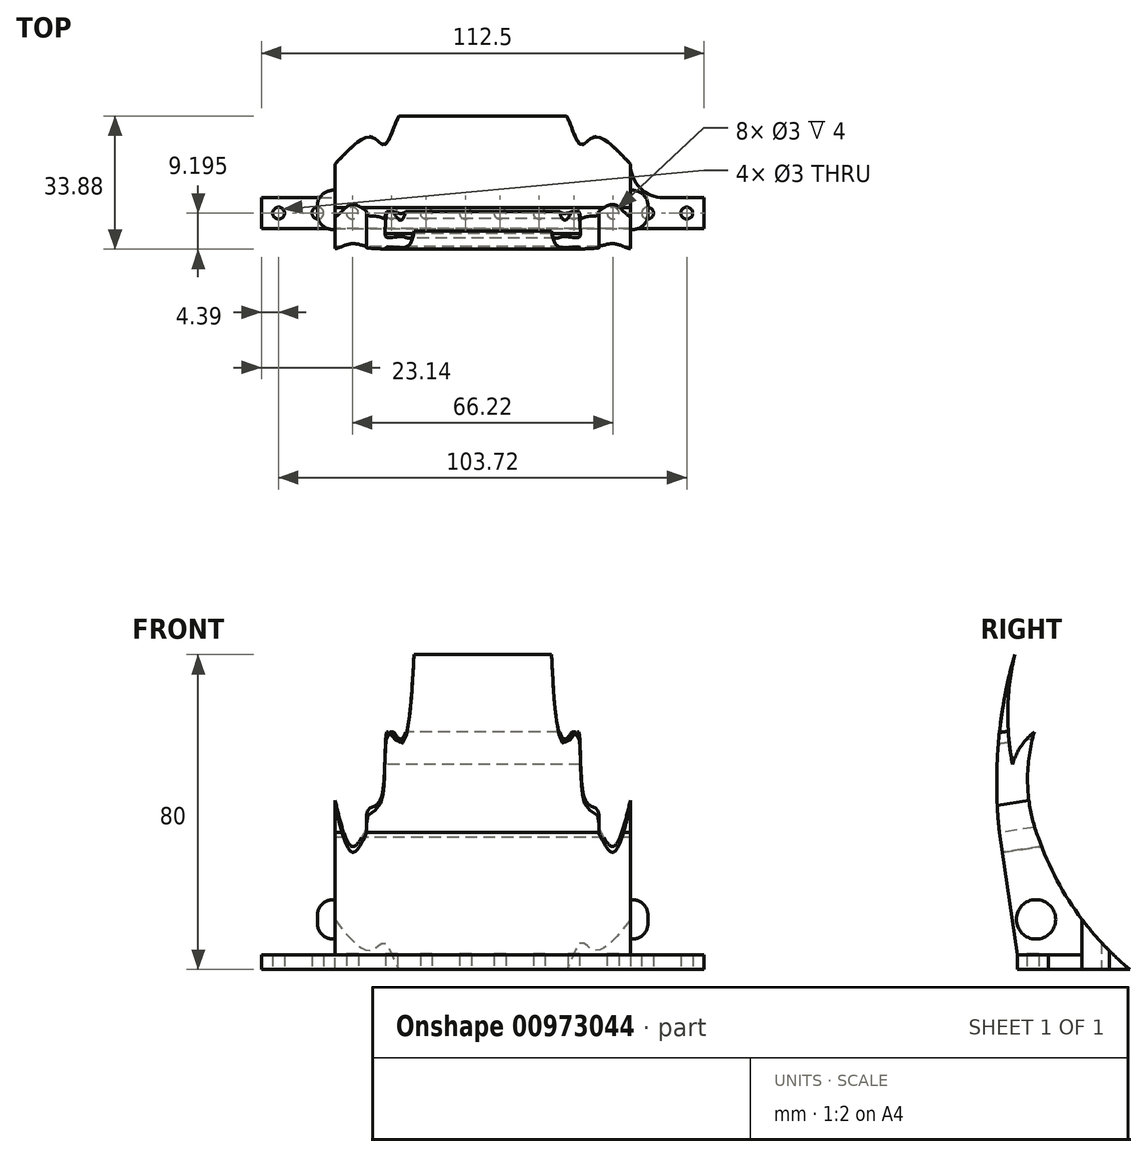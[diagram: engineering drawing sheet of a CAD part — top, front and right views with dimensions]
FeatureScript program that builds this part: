
annotation { "Feature Type Name" : "Feature", "Feature Type Description" : "" }
export const myFeature = defineFeature(function(context is Context, id is Id, definition is map)
    precondition{}
    {
        {
            var Q0;
            Q0=qCreatedBy(makeId("Top.planeOp"),FACE);
            var sketch = newSketch(context, id + "F0", { "sketchPlane" : qUnion([Q0])});
            skLineSegment(sketch, "E0.bottom", {"start": v(-38.78, 3.53) * mm, "end": v(73.72, 3.53) * mm});
            skLineSegment(sketch, "E0.top", {"start": v(-38.78, -4.36) * mm, "end": v(73.72, -4.36) * mm});
            skLineSegment(sketch, "E0.left", {"start": v(-38.78, 3.53) * mm, "end": v(-38.78, -4.36) * mm});
            skLineSegment(sketch, "E0.right", {"start": v(73.72, 3.53) * mm, "end": v(73.72, -4.36) * mm});
            skLineSegment(sketch, "E1", {"start": v(-20.03, 3.53) * mm, "end": v(-20.03, -4.36) * mm, "construction": true});
            skLineSegment(sketch, "E2", {"start": v(54.97, 3.53) * mm, "end": v(54.97, -4.36) * mm, "construction": true});
            skLineSegment(sketch, "E3", {"start": v(-38.78, -0.42) * mm, "end": v(73.72, -0.42) * mm, "construction": true});
            skCircle(sketch, "E4", {"center": v(-34.4, -0.42) * mm, "radius": 1.5 * mm});
            skCircle(sketch, "E5", {"center": v(-24.42, -0.42) * mm, "radius": 1.5 * mm});
            skCircle(sketch, "E6", {"center": v(59.36, -0.42) * mm, "radius": 1.5 * mm});
            skCircle(sketch, "E7", {"center": v(69.33, -0.42) * mm, "radius": 1.5 * mm});
            skLineSegment(sketch, "E8", {"start": v(-29.4, 3.53) * mm, "end": v(-29.4, -4.36) * mm, "construction": true});
            skLineSegment(sketch, "E9", {"start": v(-20.03, 3.53) * mm, "end": v(-38.78, 3.53) * mm});
            skLineSegment(sketch, "E10", {"start": v(54.97, 3.53) * mm, "end": v(73.72, 3.53) * mm, "construction": true});
            skLineSegment(sketch, "E11", {"start": v(64.35, 3.53) * mm, "end": v(64.35, -4.36) * mm, "construction": true});
            skLineSegment(sketch, "E12", {"start": v(-32.9, -0.42) * mm, "end": v(-25.92, -0.42) * mm});
            skPoint(sketch, "E13", {"position": v(-29.4, -0.42) * mm});
            skLineSegment(sketch, "E14", {"start": v(60.86, -0.42) * mm, "end": v(67.83, -0.42) * mm, "construction": true});
            skPoint(sketch, "E15", {"position": v(64.35, -0.42) * mm});
            skCircle(sketch, "E16.1.0.0", {"center": v(-15.64, -0.42) * mm, "radius": 1.5 * mm});
            skCircle(sketch, "E16.1.0.1", {"center": v(-5.67, -0.42) * mm, "radius": 1.5 * mm});
            skCircle(sketch, "E16.2.0.0", {"center": v(3.1, -0.42) * mm, "radius": 1.5 * mm});
            skCircle(sketch, "E16.2.0.1", {"center": v(13.08, -0.42) * mm, "radius": 1.5 * mm});
            skCircle(sketch, "E16.3.0.0", {"center": v(21.86, -0.42) * mm, "radius": 1.5 * mm});
            skCircle(sketch, "E16.3.0.1", {"center": v(31.83, -0.42) * mm, "radius": 1.5 * mm});
            skCircle(sketch, "E16.4.0.0", {"center": v(40.6, -0.42) * mm, "radius": 1.5 * mm});
            skCircle(sketch, "E16.4.0.1", {"center": v(50.58, -0.42) * mm, "radius": 1.5 * mm});
            skLineSegment(sketch, "E16.direction1", {"start": v(-34.4, -0.42) * mm, "end": v(-15.64, -0.42) * mm, "construction": true});
            skSolve(sketch);
        }
        {
            var Q0;
            Q0 = qSketchRegion(id + "F0", true);
            extrude(context, id + "F1", {"entities" : qUnion([Q0]), "depth" : 3.75 * mm, "offsetDistance" : 25 * mm});
        }
        {
            var Q0;
            Q0=makeQuery(id+"F1.opExtrude","CAP_FACE",FACE,{"disambiguationData":[OSD([sQuery(id+"F0.wireOp",EDGE,"E0.bottom"),sQuery(id+"F0.wireOp",EDGE,"E0.top"),sQuery(id+"F0.wireOp",EDGE,"E0.left"),sQuery(id+"F0.wireOp",EDGE,"E0.right"),sQuery(id+"F0.wireOp",EDGE,"E4"),sQuery(id+"F0.wireOp",EDGE,"E5"),sQuery(id+"F0.wireOp",EDGE,"E6"),sQuery(id+"F0.wireOp",EDGE,"E7"),sQuery(id+"F0.wireOp",EDGE,"E9")])],"isStart":false});
            var sketch = newSketch(context, id + "F2", { "sketchPlane" : qUnion([Q0])});
            skLineSegment(sketch, "E17.bottom", {"start": v(-20.03, 3.53) * mm, "end": v(54.97, 3.53) * mm});
            skLineSegment(sketch, "E17.top", {"start": v(-20.03, -4.36) * mm, "end": v(54.97, -4.36) * mm});
            skLineSegment(sketch, "E17.left", {"start": v(-20.03, 3.53) * mm, "end": v(-20.03, -4.36) * mm});
            skLineSegment(sketch, "E17.right", {"start": v(54.97, 3.53) * mm, "end": v(54.97, -4.36) * mm});
            skSolve(sketch);
        }
        {
            var Q0;
            Q0 = qSketchRegion(id + "F2", true);
            extrude(context, id + "F3", {"entities" : qUnion([Q0]), "operationType" : NewBodyOperationType.ADD, "depth" : 10 * mm, "offsetDistance" : 25 * mm});
        }
        {
            var Q0;
            Q0=makeQuery(id+"F3.boolean.opBoolean","MERGE",FACE,{"derivedFrom":[makeQuery(id+"F1.opExtrude","SWEPT_FACE",FACE,{"disambiguationData":[OSD([sQuery(id+"F0.wireOp",EDGE,"E0.bottom"),sQuery(id+"F0.wireOp",EDGE,"E9")])]}),makeQuery(id+"F3.opExtrude","SWEPT_FACE",FACE,{"disambiguationData":[OSD([sQuery(id+"F2.wireOp",EDGE,"E17.bottom")])]})]});
            var sketch = newSketch(context, id + "F4", { "sketchPlane" : qUnion([Q0])});
            skLineSegment(sketch, "E18.bottom", {"start": v(-54.97, 13.75) * mm, "end": v(20.03, 13.75) * mm});
            skLineSegment(sketch, "E18.top", {"start": v(-54.97, 0) * mm, "end": v(20.03, 0) * mm});
            skLineSegment(sketch, "E18.left", {"start": v(20.03, 0) * mm, "end": v(20.03, 13.75) * mm});
            skLineSegment(sketch, "E18.right", {"start": v(-54.97, 0) * mm, "end": v(-54.97, 13.75) * mm});
            skSolve(sketch);
        }
        {
            var Q0;
            Q0 = qSketchRegion(id + "F4", true);
            extrude(context, id + "F5", {"entities" : qUnion([Q0]), "operationType" : NewBodyOperationType.ADD, "depth" : 25 * mm, "offsetDistance" : 25 * mm});
        }
        {
            var Q0;
            Q0=makeQuery(id+"F5.boolean.opBoolean","MERGE",FACE,{"derivedFrom":[makeQuery(id+"F3.opExtrude","SWEPT_FACE",FACE,{"disambiguationData":[OSD([sQuery(id+"F2.wireOp",EDGE,"E17.left")])]}),makeQuery(id+"F5.opExtrude","SWEPT_FACE",FACE,{"disambiguationData":[OSD([sQuery(id+"F4.wireOp",EDGE,"E18.left")])]})]});
            var sketch = newSketch(context, id + "F6", { "sketchPlane" : qUnion([Q0])});
            skFitSpline(sketch, "E19", {"points": [v(-28.53, 0) * mm, v(-27.7, 3) * mm, v(-21.04, 9.75) * mm, v(-22.48, 11.13) * mm, v(-12.08, 13.75) * mm], "startDerivative": vector(-1.4, 14.45) * mm, "endDerivative": vector(46.88, 7.86) * mm});
            skSolve(sketch);
        }
        {
            var Q0;
            {var subQ0=sQuery(id+"F6.wireOp",EDGE,"E19");var subQ1=sQuery(id+"F4.wireOp",EDGE,"E18.left");var subQ4=makeQuery(id+"F5.opExtrude","CAP_EDGE",EDGE,{"disambiguationData":[OSD([subQ1])],"isStart":false});var subQ5=makeQuery(id+"F6.imprint","INTERSECT",VERTEX,{"derivedFrom":[subQ4,subQ0]});Q0=makeQuery(id+"F6.imprint","IMPRINT",FACE,{"disambiguationData":[TD([[makeQuery(id+"F6.imprint","IMPRINT",EDGE,{"disambiguationData":[TD([[subQ5,-1.0]])],"derivedFrom":subQ0}),1.0]])]});}
            extrude(context, id + "F7", {"entities" : qUnion([Q0]), "operationType" : NewBodyOperationType.REMOVE, "oppositeDirection" : true, "depth" : 108.8 * mm, "offsetDistance" : 25 * mm});
        }
        {
            var Q0;
            Q0=makeQuery(id+"F5.boolean.opBoolean","MERGE",FACE,{"derivedFrom":[makeQuery(id+"F3.opExtrude","CAP_FACE",FACE,{"disambiguationData":[OSD([sQuery(id+"F2.wireOp",EDGE,"E17.bottom"),sQuery(id+"F2.wireOp",EDGE,"E17.top"),sQuery(id+"F2.wireOp",EDGE,"E17.left"),sQuery(id+"F2.wireOp",EDGE,"E17.right")])],"isStart":false}),makeQuery(id+"F5.opExtrude","SWEPT_FACE",FACE,{"disambiguationData":[OSD([sQuery(id+"F4.wireOp",EDGE,"E18.bottom")])]})]});
            var sketch = newSketch(context, id + "F8", { "sketchPlane" : qUnion([Q0])});
            skFitSpline(sketch, "E20", {"points": [v(-20.03, 12.08) * mm, v(-10.74, 18.9) * mm, v(-7.44, 17) * mm, v(-1.88, 26.86) * mm, v(6.82, 24.75) * mm, v(17.47, 28.53) * mm], "startDerivative": vector(45.64, 47.07) * mm, "endDerivative": vector(40.7, 21.22) * mm});
            skLineSegment(sketch, "E21", {"start": v(17.47, -4.36) * mm, "end": v(17.47, 28.53) * mm, "construction": true});
            skFitSpline(sketch, "E22.MirrorCS", {"points": [v(54.97, 12.08) * mm, v(45.68, 18.9) * mm, v(42.38, 17) * mm, v(36.82, 26.86) * mm, v(28.12, 24.75) * mm, v(17.47, 28.53) * mm], "startDerivative": vector(-45.64, 47.07) * mm, "endDerivative": vector(-40.7, 21.22) * mm});
            skLineSegment(sketch, "E23.0", {"start": v(54.97, 28.53) * mm, "end": v(-20.03, 28.53) * mm});
            skLineSegment(sketch, "E24.0", {"start": v(54.97, 28.53) * mm, "end": v(54.97, 3.53) * mm});
            skLineSegment(sketch, "E24.1", {"start": v(-20.03, 28.53) * mm, "end": v(-20.03, 3.53) * mm});
            skSolve(sketch);
        }
        {
            var Q0;
            Q0 = qSketchRegion(id + "F8", true);
            extrude(context, id + "F9", {"entities" : qUnion([Q0]), "operationType" : NewBodyOperationType.REMOVE, "oppositeDirection" : true, "depth" : 25 * mm, "offsetDistance" : 25 * mm});
        }
        {
            var Q0;
            Q0=makeQuery(id+"F5.boolean.opBoolean","MERGE",FACE,{"derivedFrom":[makeQuery(id+"F3.opExtrude","CAP_FACE",FACE,{"disambiguationData":[OSD([sQuery(id+"F2.wireOp",EDGE,"E17.bottom"),sQuery(id+"F2.wireOp",EDGE,"E17.top"),sQuery(id+"F2.wireOp",EDGE,"E17.left"),sQuery(id+"F2.wireOp",EDGE,"E17.right")])],"isStart":false}),makeQuery(id+"F5.opExtrude","SWEPT_FACE",FACE,{"disambiguationData":[OSD([sQuery(id+"F4.wireOp",EDGE,"E18.bottom")])]})]});
            var sketch = newSketch(context, id + "F10", { "sketchPlane" : qUnion([Q0])});
            skLineSegment(sketch, "E25.bottom", {"start": v(-6.29, -4.36) * mm, "end": v(40.42, -4.36) * mm});
            skLineSegment(sketch, "E25.top", {"start": v(-6.29, 12.08) * mm, "end": v(40.42, 12.08) * mm, "construction": true});
            skLineSegment(sketch, "E25.left", {"start": v(-6.29, -4.36) * mm, "end": v(-6.29, 12.08) * mm});
            skLineSegment(sketch, "E25.right", {"start": v(40.42, -4.36) * mm, "end": v(40.42, 12.08) * mm});
            skLineSegment(sketch, "E26", {"start": v(-6.29, 12.08) * mm, "end": v(17.07, 17.99) * mm});
            skLineSegment(sketch, "E27", {"start": v(17.07, 17.99) * mm, "end": v(40.42, 12.08) * mm});
            skLineSegment(sketch, "E28", {"start": v(17.07, -4.36) * mm, "end": v(17.07, 30.33) * mm});
            skSolve(sketch);
        }
        {
            var Q0;
            {var subQ0=sQuery(id+"F10.wireOp",EDGE,"E25.right");Q0=makeQuery(id+"F10.imprint","IMPRINT",FACE,{"disambiguationData":[TD([[makeQuery(id+"F10.imprint","IMPRINT",EDGE,{"derivedFrom":subQ0}),1.0]])]});}
            var Q1;
            {var subQ0=sQuery(id+"F10.wireOp",EDGE,"E25.left");Q1=makeQuery(id+"F10.imprint","IMPRINT",FACE,{"disambiguationData":[TD([[makeQuery(id+"F10.imprint","IMPRINT",EDGE,{"derivedFrom":subQ0}),-1.0]])]});}
            var Q2;
            {var subQ0=sQuery(id+"F10.wireOp",EDGE,"E27");Q2=makeQuery(id+"F10.imprint","IMPRINT",FACE,{"disambiguationData":[TD([[makeQuery(id+"F10.imprint","IMPRINT",EDGE,{"derivedFrom":subQ0}),-1.0]])]});}
            var Q3;
            {var subQ0=sQuery(id+"F10.wireOp",EDGE,"E26");Q3=makeQuery(id+"F10.imprint","IMPRINT",FACE,{"disambiguationData":[TD([[makeQuery(id+"F10.imprint","IMPRINT",EDGE,{"derivedFrom":subQ0}),-1.0]])]});}
            extrude(context, id + "F11", {"entities" : qUnion([Q0, Q1, Q2, Q3]), "operationType" : NewBodyOperationType.ADD, "depth" : 5 * mm, "offsetDistance" : 25 * mm});
        }
        {
            var Q0;
            Q0=makeQuery(id+"F11.opExtrude","CAP_EDGE",EDGE,{"disambiguationData":[OSD([sQuery(id+"F10.wireOp",EDGE,"E25.left")])],"isStart":true});
            var Q1;
            Q1=makeQuery(id+"F11.opExtrude","CAP_EDGE",EDGE,{"disambiguationData":[OSD([sQuery(id+"F10.wireOp",EDGE,"E25.right")])],"isStart":true});
            fillet(context, id + "F12", {"entities" : qUnion([Q0, Q1]), "radius" : 21.25 * mm, "tangentPropagation" : true, "allowEdgeOverflow" : false});
        }
        {
            var Q0;
            {var subQ0=sQuery(id+"F10.wireOp",EDGE,"E25.left");Q0=makeQuery(id+"F12.opFillet","BLEND_EDGE",EDGE,{"blendedFrom":[makeQuery(id+"F11.opExtrude","CAP_EDGE",EDGE,{"disambiguationData":[OSD([subQ0])],"isStart":true}),makeQuery(id+"F11.opExtrude","CAP_FACE",FACE,{"disambiguationData":[OSD([sQuery(id+"F10.wireOp",EDGE,"E25.bottom"),subQ0,sQuery(id+"F10.wireOp",EDGE,"E25.right"),sQuery(id+"F10.wireOp",EDGE,"E26"),sQuery(id+"F10.wireOp",EDGE,"E27")])],"isStart":false})],"blendedInto":[makeQuery(id+"F11.opExtrude","CAP_FACE",FACE,{"disambiguationData":[OSD([sQuery(id+"F10.wireOp",EDGE,"E25.bottom"),subQ0,sQuery(id+"F10.wireOp",EDGE,"E25.right"),sQuery(id+"F10.wireOp",EDGE,"E26"),sQuery(id+"F10.wireOp",EDGE,"E27")])],"isStart":false})]});}
            var Q1;
            {var subQ0=sQuery(id+"F10.wireOp",EDGE,"E26");Q1=makeQuery(id+"FigYtTYyMIsJvTv_1.opChamfer","BLEND_EDGE",EDGE,{"blendedFrom":[makeQuery(id+"F11.opExtrude","CAP_EDGE",EDGE,{"disambiguationData":[OSD([subQ0])],"isStart":false}),makeQuery(id+"F11.opExtrude","CAP_FACE",FACE,{"disambiguationData":[OSD([sQuery(id+"F10.wireOp",EDGE,"E25.bottom"),sQuery(id+"F10.wireOp",EDGE,"E25.left"),sQuery(id+"F10.wireOp",EDGE,"E25.right"),subQ0,sQuery(id+"F10.wireOp",EDGE,"E27")])],"isStart":false})],"blendedInto":[makeQuery(id+"F11.opExtrude","CAP_FACE",FACE,{"disambiguationData":[OSD([sQuery(id+"F10.wireOp",EDGE,"E25.bottom"),sQuery(id+"F10.wireOp",EDGE,"E25.left"),sQuery(id+"F10.wireOp",EDGE,"E25.right"),subQ0,sQuery(id+"F10.wireOp",EDGE,"E27")])],"isStart":false})]});}
            var Q2;
            {var subQ0=sQuery(id+"F10.wireOp",EDGE,"E27");Q2=makeQuery(id+"FigYtTYyMIsJvTv_1.opChamfer","BLEND_EDGE",EDGE,{"blendedFrom":[makeQuery(id+"F11.opExtrude","CAP_EDGE",EDGE,{"disambiguationData":[OSD([subQ0])],"isStart":false}),makeQuery(id+"F11.opExtrude","CAP_FACE",FACE,{"disambiguationData":[OSD([sQuery(id+"F10.wireOp",EDGE,"E25.bottom"),sQuery(id+"F10.wireOp",EDGE,"E25.left"),sQuery(id+"F10.wireOp",EDGE,"E25.right"),sQuery(id+"F10.wireOp",EDGE,"E26"),subQ0])],"isStart":false})],"blendedInto":[makeQuery(id+"F11.opExtrude","CAP_FACE",FACE,{"disambiguationData":[OSD([sQuery(id+"F10.wireOp",EDGE,"E25.bottom"),sQuery(id+"F10.wireOp",EDGE,"E25.left"),sQuery(id+"F10.wireOp",EDGE,"E25.right"),sQuery(id+"F10.wireOp",EDGE,"E26"),subQ0])],"isStart":false})]});}
            var Q3;
            {var subQ0=sQuery(id+"F10.wireOp",EDGE,"E25.right");Q3=makeQuery(id+"F12.opFillet","BLEND_EDGE",EDGE,{"blendedFrom":[makeQuery(id+"F11.opExtrude","CAP_EDGE",EDGE,{"disambiguationData":[OSD([subQ0])],"isStart":true}),makeQuery(id+"F11.opExtrude","CAP_FACE",FACE,{"disambiguationData":[OSD([sQuery(id+"F10.wireOp",EDGE,"E25.bottom"),sQuery(id+"F10.wireOp",EDGE,"E25.left"),subQ0,sQuery(id+"F10.wireOp",EDGE,"E26"),sQuery(id+"F10.wireOp",EDGE,"E27")])],"isStart":false})],"blendedInto":[makeQuery(id+"F11.opExtrude","CAP_FACE",FACE,{"disambiguationData":[OSD([sQuery(id+"F10.wireOp",EDGE,"E25.bottom"),sQuery(id+"F10.wireOp",EDGE,"E25.left"),subQ0,sQuery(id+"F10.wireOp",EDGE,"E26"),sQuery(id+"F10.wireOp",EDGE,"E27")])],"isStart":false})]});}
            fillet(context, id + "F13", {"entities" : qUnion([Q0, Q1, Q2, Q3]), "radius" : 8 * mm, "tangentPropagation" : true, "allowEdgeOverflow" : false});
        }
        {
            var Q0;
            Q0=makeQuery(id+"F5.boolean.opBoolean","MERGE",FACE,{"derivedFrom":[makeQuery(id+"F3.opExtrude","SWEPT_FACE",FACE,{"disambiguationData":[OSD([sQuery(id+"F2.wireOp",EDGE,"E17.left")])]}),makeQuery(id+"F5.opExtrude","SWEPT_FACE",FACE,{"disambiguationData":[OSD([sQuery(id+"F4.wireOp",EDGE,"E18.left")])]})]});
            var sketch = newSketch(context, id + "F14", { "sketchPlane" : qUnion([Q0])});
            skLineSegment(sketch, "E29", {"start": v(4.36, 3.75) * mm, "end": v(8.92, 34.79) * mm});
            skArc(sketch, "E30", {"start": v(8.92, 34.79) * mm, "mid": v(9.18, 57.58) * mm, "end": v(5, 80) * mm});
            skArc(sketch, "E31", {"start": v(-16.96, 13.75) * mm, "mid": v(3.4, 43.77) * mm, "end": v(5, 80) * mm});
            skArc(sketch, "E32", {"start": v(-0.96, 33.55) * mm, "mid": v(1.74, 46.91) * mm, "end": v(0, 60.43) * mm});
            skArc(sketch, "E33", {"start": v(5.58, 52.1) * mm, "mid": v(3.44, 56.7) * mm, "end": v(0, 60.43) * mm});
            skLineSegment(sketch, "E34", {"start": v(-16.96, 13.75) * mm, "end": v(-5.96, 13.75) * mm});
            skLineSegment(sketch, "E35", {"start": v(-5.96, 13.75) * mm, "end": v(-5.96, 0) * mm});
            skLineSegment(sketch, "E36", {"start": v(-5.96, 0) * mm, "end": v(4.36, 0) * mm});
            skLineSegment(sketch, "E37", {"start": v(4.36, 0) * mm, "end": v(4.36, 3.75) * mm});
            skSolve(sketch);
        }
        {
            var Q0;
            Q0 = qSketchRegion(id + "F14", true);
            extrude(context, id + "F15", {"entities" : qUnion([Q0]), "operationType" : NewBodyOperationType.ADD, "oppositeDirection" : true, "depth" : 75 * mm, "offsetDistance" : 25 * mm});
        }
        {
            var Q0;
            Q0=makeQuery(id+"F15.opExtrude","SWEPT_FACE",FACE,{"disambiguationData":[OSD([sQuery(id+"F14.wireOp",EDGE,"E29")])]});
            var sketch = newSketch(context, id + "F16", { "sketchPlane" : qUnion([Q0])});
            skFitSpline(sketch, "E38", {"points": [v(0, 79.88) * mm, v(-3.73, 58.12) * mm, v(-6.47, 60.86) * mm, v(-8.59, 42.78) * mm, v(-11.43, 40.55) * mm, v(-11.99, 35.71) * mm], "startDerivative": vector(-6.1, -121.82) * mm, "endDerivative": vector(2.52, -42.33) * mm});
            skLineSegment(sketch, "E39", {"start": v(17.47, 4.34) * mm, "end": v(17.47, 79.88) * mm, "construction": true});
            skFitSpline(sketch, "E40.MirrorCS", {"points": [v(34.94, 79.88) * mm, v(38.67, 58.12) * mm, v(41.4, 60.86) * mm, v(43.53, 42.78) * mm, v(46.37, 40.55) * mm, v(46.93, 35.71) * mm], "startDerivative": vector(6.1, -121.82) * mm, "endDerivative": vector(-2.52, -42.33) * mm});
            skFitSpline(sketch, "E41", {"points": [v(-11.99, 35.71) * mm, v(-15.59, 30.67) * mm, v(-20.03, 42.66) * mm], "startDerivative": vector(-9.04, -18.97) * mm, "endDerivative": vector(-7.02, 29.96) * mm});
            skFitSpline(sketch, "E42.MirrorCS", {"points": [v(46.93, 35.71) * mm, v(50.53, 30.67) * mm, v(54.97, 42.66) * mm], "startDerivative": vector(9.04, -18.97) * mm, "endDerivative": vector(7.02, 29.96) * mm});
            skLineSegment(sketch, "E43.0", {"start": v(54.97, 79.88) * mm, "end": v(-20.03, 79.88) * mm});
            skLineSegment(sketch, "E43.1", {"start": v(-20.03, 35.71) * mm, "end": v(-20.03, 79.88) * mm});
            skLineSegment(sketch, "E43.2", {"start": v(54.97, 35.71) * mm, "end": v(54.97, 79.88) * mm});
            skSolve(sketch);
        }
        {
            var Q0;
            Q0 = qSketchRegion(id + "F16", true);
            extrude(context, id + "F17", {"entities" : qUnion([Q0]), "operationType" : NewBodyOperationType.REMOVE, "oppositeDirection" : true, "depth" : 25 * mm, "offsetDistance" : 25 * mm});
        }
        {
            var Q0;
            Q0=makeQuery(id+"F11.opExtrude","CAP_FACE",FACE,{"disambiguationData":[OSD([sQuery(id+"F10.wireOp",EDGE,"E25.bottom"),sQuery(id+"F10.wireOp",EDGE,"E25.left"),sQuery(id+"F10.wireOp",EDGE,"E25.right"),sQuery(id+"F10.wireOp",EDGE,"E26"),sQuery(id+"F10.wireOp",EDGE,"E27")])],"isStart":false});
            var sketch = newSketch(context, id + "F18", { "sketchPlane" : qUnion([Q0])});
            skSolve(sketch);
        }
        {
            var Q0;
            Q0=makeQuery(id+"F5.opExtrude","CAP_EDGE",EDGE,{"disambiguationData":[OSD([sQuery(id+"F4.wireOp",EDGE,"E18.right")])],"isStart":true});
            var Q1;
            Q1=makeQuery(id+"F5.opExtrude","CAP_EDGE",EDGE,{"disambiguationData":[OSD([sQuery(id+"F4.wireOp",EDGE,"E18.left")])],"isStart":true});
            fillet(context, id + "F19", {"entities" : qUnion([Q0, Q1]), "radius" : 8.45 * mm, "tangentPropagation" : true, "allowEdgeOverflow" : false});
        }
        {
            var Q0;
            Q0=makeQuery(id+"F0.imprint","IMPRINT",FACE,{"disambiguationData":[TD([[makeQuery(id+"F0.imprint","IMPRINT",EDGE,{"derivedFrom":sQuery(id+"F0.wireOp",EDGE,"E16.1.0.0")}),1.0]])]});
            var Q1;
            Q1=makeQuery(id+"F0.imprint","IMPRINT",FACE,{"disambiguationData":[TD([[makeQuery(id+"F0.imprint","IMPRINT",EDGE,{"derivedFrom":sQuery(id+"F0.wireOp",EDGE,"E16.1.0.1")}),1.0]])]});
            var Q2;
            Q2=makeQuery(id+"F0.imprint","IMPRINT",FACE,{"disambiguationData":[TD([[makeQuery(id+"F0.imprint","IMPRINT",EDGE,{"derivedFrom":sQuery(id+"F0.wireOp",EDGE,"E16.2.0.0")}),1.0]])]});
            var Q3;
            Q3=makeQuery(id+"F0.imprint","IMPRINT",FACE,{"disambiguationData":[TD([[makeQuery(id+"F0.imprint","IMPRINT",EDGE,{"derivedFrom":sQuery(id+"F0.wireOp",EDGE,"E16.2.0.1")}),1.0]])]});
            var Q4;
            Q4=makeQuery(id+"F0.imprint","IMPRINT",FACE,{"disambiguationData":[TD([[makeQuery(id+"F0.imprint","IMPRINT",EDGE,{"derivedFrom":sQuery(id+"F0.wireOp",EDGE,"E16.3.0.0")}),1.0]])]});
            var Q5;
            Q5=makeQuery(id+"F0.imprint","IMPRINT",FACE,{"disambiguationData":[TD([[makeQuery(id+"F0.imprint","IMPRINT",EDGE,{"derivedFrom":sQuery(id+"F0.wireOp",EDGE,"E16.3.0.1")}),1.0]])]});
            var Q6;
            Q6=makeQuery(id+"F0.imprint","IMPRINT",FACE,{"disambiguationData":[TD([[makeQuery(id+"F0.imprint","IMPRINT",EDGE,{"derivedFrom":sQuery(id+"F0.wireOp",EDGE,"E16.4.0.1")}),1.0]])]});
            var Q7;
            Q7=makeQuery(id+"F0.imprint","IMPRINT",FACE,{"disambiguationData":[TD([[makeQuery(id+"F0.imprint","IMPRINT",EDGE,{"derivedFrom":sQuery(id+"F0.wireOp",EDGE,"E16.4.0.0")}),1.0]])]});
            extrude(context, id + "F20", {"entities" : qUnion([Q0, Q1, Q2, Q3, Q4, Q5, Q6, Q7]), "operationType" : NewBodyOperationType.REMOVE, "depth" : 4 * mm, "offsetDistance" : 25 * mm});
        }
        {
            var Q0;
            Q0=makeQuery(id+"F15.boolean.opBoolean","MERGE",FACE,{"derivedFrom":[makeQuery(id+"F5.boolean.opBoolean","MERGE",FACE,{"derivedFrom":[makeQuery(id+"F3.opExtrude","SWEPT_FACE",FACE,{"disambiguationData":[OSD([sQuery(id+"F2.wireOp",EDGE,"E17.left")])]}),makeQuery(id+"F5.opExtrude","SWEPT_FACE",FACE,{"disambiguationData":[OSD([sQuery(id+"F4.wireOp",EDGE,"E18.left")])]})]}),makeQuery(id+"F15.opExtrude","CAP_FACE",FACE,{"disambiguationData":[OSD([sQuery(id+"F14.wireOp",EDGE,"E29"),sQuery(id+"F14.wireOp",EDGE,"E30"),sQuery(id+"F14.wireOp",EDGE,"E31"),sQuery(id+"F14.wireOp",EDGE,"E32"),sQuery(id+"F14.wireOp",EDGE,"E33"),sQuery(id+"F14.wireOp",EDGE,"E34"),sQuery(id+"F14.wireOp",EDGE,"E35"),sQuery(id+"F14.wireOp",EDGE,"E36"),sQuery(id+"F14.wireOp",EDGE,"E37")])],"isStart":true})]});
            var sketch = newSketch(context, id + "F21", { "sketchPlane" : qUnion([Q0])});
            skArc(sketch, "E44", {"start": v(-24.27, 0) * mm, "mid": v(-10.31, 15.18) * mm, "end": v(-0.96, 33.55) * mm});
            skLineSegment(sketch, "E45", {"start": v(-0.96, 33.55) * mm, "end": v(-34.58, 33.55) * mm});
            skLineSegment(sketch, "E46", {"start": v(-34.58, 33.55) * mm, "end": v(-34.58, 0) * mm});
            skLineSegment(sketch, "E47", {"start": v(-34.58, 0) * mm, "end": v(-24.27, 0) * mm});
            skSolve(sketch);
        }
        {
            var Q0;
            Q0 = qSketchRegion(id + "F21", true);
            extrude(context, id + "F22", {"entities" : qUnion([Q0]), "operationType" : NewBodyOperationType.REMOVE, "oppositeDirection" : true, "depth" : 113.6 * mm, "offsetDistance" : 25 * mm});
        }
        {
            var Q0;
            Q0=makeQuery(id+"F15.boolean.opBoolean","MERGE",FACE,{"derivedFrom":[makeQuery(id+"F5.boolean.opBoolean","MERGE",FACE,{"derivedFrom":[makeQuery(id+"F3.opExtrude","SWEPT_FACE",FACE,{"disambiguationData":[OSD([sQuery(id+"F2.wireOp",EDGE,"E17.right")])]}),makeQuery(id+"F5.opExtrude","SWEPT_FACE",FACE,{"disambiguationData":[OSD([sQuery(id+"F4.wireOp",EDGE,"E18.right")])]})]}),makeQuery(id+"F15.opExtrude","CAP_FACE",FACE,{"disambiguationData":[OSD([sQuery(id+"F14.wireOp",EDGE,"E29"),sQuery(id+"F14.wireOp",EDGE,"E30"),sQuery(id+"F14.wireOp",EDGE,"E31"),sQuery(id+"F14.wireOp",EDGE,"E32"),sQuery(id+"F14.wireOp",EDGE,"E33"),sQuery(id+"F14.wireOp",EDGE,"E34"),sQuery(id+"F14.wireOp",EDGE,"E35"),sQuery(id+"F14.wireOp",EDGE,"E36"),sQuery(id+"F14.wireOp",EDGE,"E37")])],"isStart":false})]});
            var sketch = newSketch(context, id + "F23", { "sketchPlane" : qUnion([Q0])});
            skCircle(sketch, "E48", {"center": v(0.38, 12.75) * mm, "radius": 5 * mm});
            skSolve(sketch);
        }
        {
            var Q0;
            Q0 = qSketchRegion(id + "F23", true);
            extrude(context, id + "F24", {"entities" : qUnion([Q0]), "operationType" : NewBodyOperationType.ADD, "depth" : 4.5 * mm, "offsetDistance" : 25 * mm});
        }
        {
            var Q0;
            Q0=makeQuery(id+"F24.opExtrude","CAP_EDGE",EDGE,{"disambiguationData":[OSD([sQuery(id+"F23.wireOp",EDGE,"E48")])],"isStart":false});
            fillet(context, id + "F25", {"entities" : qUnion([Q0]), "radius" : 4 * mm, "tangentPropagation" : true, "allowEdgeOverflow" : false});
        }
        {
            var Q0;
            Q0=makeQuery(id+"F15.boolean.opBoolean","MERGE",FACE,{"derivedFrom":[makeQuery(id+"F5.boolean.opBoolean","MERGE",FACE,{"derivedFrom":[makeQuery(id+"F3.opExtrude","SWEPT_FACE",FACE,{"disambiguationData":[OSD([sQuery(id+"F2.wireOp",EDGE,"E17.left")])]}),makeQuery(id+"F5.opExtrude","SWEPT_FACE",FACE,{"disambiguationData":[OSD([sQuery(id+"F4.wireOp",EDGE,"E18.left")])]})]}),makeQuery(id+"F15.opExtrude","CAP_FACE",FACE,{"disambiguationData":[OSD([sQuery(id+"F14.wireOp",EDGE,"E29"),sQuery(id+"F14.wireOp",EDGE,"E30"),sQuery(id+"F14.wireOp",EDGE,"E31"),sQuery(id+"F14.wireOp",EDGE,"E32"),sQuery(id+"F14.wireOp",EDGE,"E33"),sQuery(id+"F14.wireOp",EDGE,"E34"),sQuery(id+"F14.wireOp",EDGE,"E35"),sQuery(id+"F14.wireOp",EDGE,"E36"),sQuery(id+"F14.wireOp",EDGE,"E37")])],"isStart":true})]});
            var sketch = newSketch(context, id + "F26", { "sketchPlane" : qUnion([Q0])});
            skCircle(sketch, "E49.0", {"center": v(-0.38, 12.75) * mm, "radius": 5 * mm});
            skSolve(sketch);
        }
        {
            var Q0;
            Q0 = qSketchRegion(id + "F26", true);
            extrude(context, id + "F27", {"entities" : qUnion([Q0]), "operationType" : NewBodyOperationType.ADD, "depth" : 4.5 * mm, "offsetDistance" : 25 * mm});
        }
        {
            var Q0;
            Q0=makeQuery(id+"F27.opExtrude","CAP_EDGE",EDGE,{"disambiguationData":[OSD([sQuery(id+"F26.wireOp",EDGE,"E49.0")])],"isStart":false});
            fillet(context, id + "F28", {"entities" : qUnion([Q0]), "radius" : 4 * mm, "tangentPropagation" : true, "allowEdgeOverflow" : false});
        }
    });
